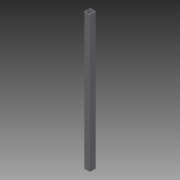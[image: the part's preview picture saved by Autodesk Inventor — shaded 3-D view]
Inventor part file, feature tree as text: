
AUTODESK INVENTOR PART (.ipt)
format: ipt  version: 2013 (Build 170138000, 138)  size: 87,040 bytes
history: native  units: in
note: dims shown in document units (in); Inventor stores cm internally (conversion verified against a paired STEP export)
features: extrude x2, sketch x2
ambient origin geometry x8: Origin, YZ Plane, XZ Plane, XY Plane, X Axis, Y Axis, Z Axis, Center Point
bodies: Solid1 (feature_tree)
feature tree (4):
  extrude  "Extrusion1"  Depth=1.0in
  extrude  "Extrusion2"  Depth=36.0in TaperAngle=0.0deg
  sketch  "Sketch1"  dims[d0=1.0in d2=1.0in]
  sketch  "Sketch2"  dims[d3=0.0625in d4=36.0in d5=0.0in d6=23.5in d7=23.5213in d8=36.0in d9=0.0in]
